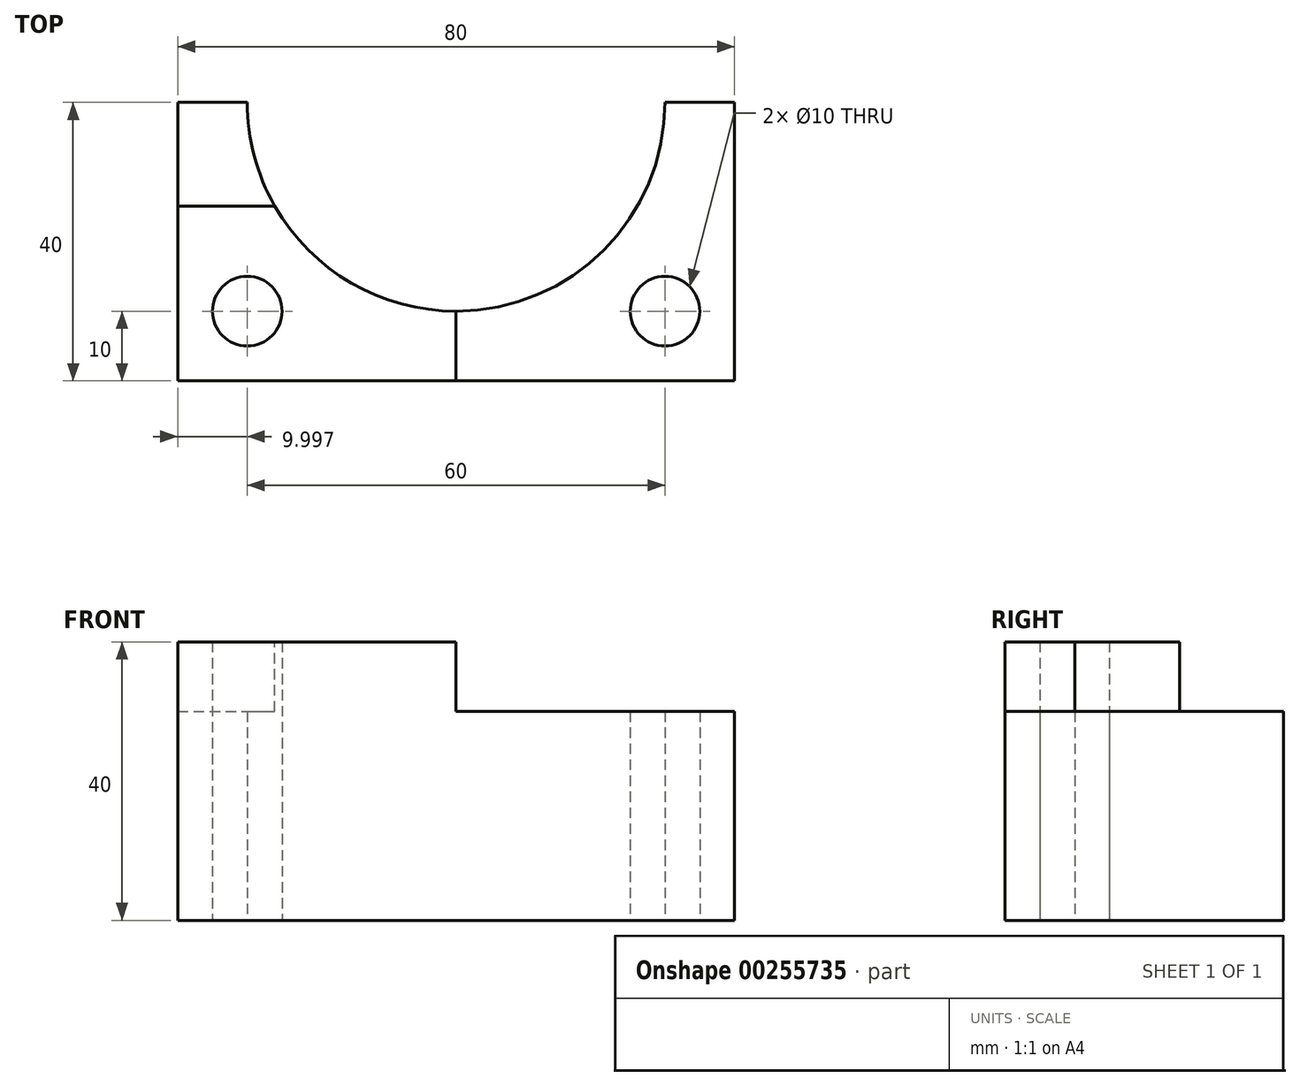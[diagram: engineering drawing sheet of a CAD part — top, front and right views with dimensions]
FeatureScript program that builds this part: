
annotation { "Feature Type Name" : "Feature", "Feature Type Description" : "" }
export const myFeature = defineFeature(function(context is Context, id is Id, definition is map)
    precondition{}
    {
        {
            var Q0;
            Q0=qCreatedBy(makeId("Top.planeOp"),FACE);
            var sketch = newSketch(context, id + "F0", { "sketchPlane" : qUnion([Q0])});
            skLineSegment(sketch, "E0.bottom", {"start": v(-49.91, 0) * mm, "end": v(30.09, 0) * mm});
            skLineSegment(sketch, "E0.top", {"start": v(-49.91, 40) * mm, "end": v(-39.91, 40) * mm});
            skLineSegment(sketch, "E0.left", {"start": v(-49.91, 0) * mm, "end": v(-49.91, 40) * mm});
            skLineSegment(sketch, "E0.right", {"start": v(30.09, 0) * mm, "end": v(30.09, 40) * mm});
            skCircle(sketch, "E1", {"center": v(-39.91, 10) * mm, "radius": 5 * mm});
            skArc(sketch, "E2", {"start": v(20.09, 40) * mm, "mid": v(-9.91, 10) * mm, "end": v(-39.91, 40) * mm});
            skCircle(sketch, "E3", {"center": v(20.09, 10) * mm, "radius": 5 * mm});
            skLineSegment(sketch, "E4.trimOffspring", {"start": v(20.09, 40) * mm, "end": v(30.09, 40) * mm});
            skSolve(sketch);
        }
        {
            var Q0;
            Q0=makeQuery(id+"F0.imprint","IMPRINT",FACE,{"disambiguationData":[TD([[makeQuery(id+"F0.imprint","IMPRINT",EDGE,{"derivedFrom":sQuery(id+"F0.wireOp",EDGE,"E0.bottom")}),1.0]])]});
            extrude(context, id + "F1", {"entities" : qUnion([Q0]), "depth" : 40 * mm});
        }
        {
            var Q0;
            Q0=makeQuery(id+"F1.opExtrude","CAP_FACE",FACE,{"disambiguationData":[OSD([sQuery(id+"F0.wireOp",EDGE,"E0.bottom"),sQuery(id+"F0.wireOp",EDGE,"E0.top"),sQuery(id+"F0.wireOp",EDGE,"E0.left"),sQuery(id+"F0.wireOp",EDGE,"E0.right"),sQuery(id+"F0.wireOp",EDGE,"E1"),sQuery(id+"F0.wireOp",EDGE,"E2"),sQuery(id+"F0.wireOp",EDGE,"E3"),sQuery(id+"F0.wireOp",EDGE,"E4.trimOffspring")])],"isStart":false});
            var sketch = newSketch(context, id + "F2", { "sketchPlane" : qUnion([Q0])});
            skLineSegment(sketch, "E5.bottom", {"start": v(-57.42, 43.27) * mm, "end": v(-30.31, 43.27) * mm});
            skLineSegment(sketch, "E5.top", {"start": v(-57.42, 25.1) * mm, "end": v(-30.31, 25.1) * mm});
            skLineSegment(sketch, "E5.left", {"start": v(-57.42, 43.27) * mm, "end": v(-57.42, 25.1) * mm});
            skLineSegment(sketch, "E5.right", {"start": v(-30.31, 43.27) * mm, "end": v(-30.31, 25.1) * mm});
            skLineSegment(sketch, "E6.bottom", {"start": v(-9.91, 0) * mm, "end": v(39.7, 0) * mm});
            skLineSegment(sketch, "E6.top", {"start": v(-9.91, 55.7) * mm, "end": v(39.7, 55.7) * mm});
            skLineSegment(sketch, "E6.left", {"start": v(-9.91, 0) * mm, "end": v(-9.91, 55.7) * mm});
            skLineSegment(sketch, "E6.right", {"start": v(39.7, 0) * mm, "end": v(39.7, 55.7) * mm});
            skSolve(sketch);
        }
        {
            var Q0;
            {var subQ5=makeQuery(id+"F1.opExtrude","CAP_EDGE",EDGE,{"disambiguationData":[OSD([sQuery(id+"F0.wireOp",EDGE,"E0.top")])],"isStart":false});Q0=makeQuery(id+"F2.imprint","IMPRINT",FACE,{"disambiguationData":[TD([[makeQuery(id+"F2.imprint","IMPRINT",EDGE,{"derivedFrom":subQ5}),-1.0]])]});}
            var Q1;
            {var subQ5=makeQuery(id+"F1.opExtrude","CAP_EDGE",EDGE,{"disambiguationData":[OSD([sQuery(id+"F0.wireOp",EDGE,"E0.right")])],"isStart":false});Q1=makeQuery(id+"F2.imprint","IMPRINT",FACE,{"disambiguationData":[TD([[makeQuery(id+"F2.imprint","IMPRINT",EDGE,{"derivedFrom":subQ5}),1.0]])]});}
            extrude(context, id + "F3", {"entities" : qUnion([Q0, Q1]), "operationType" : NewBodyOperationType.REMOVE, "oppositeDirection" : true, "depth" : 10 * mm});
        }
    });
